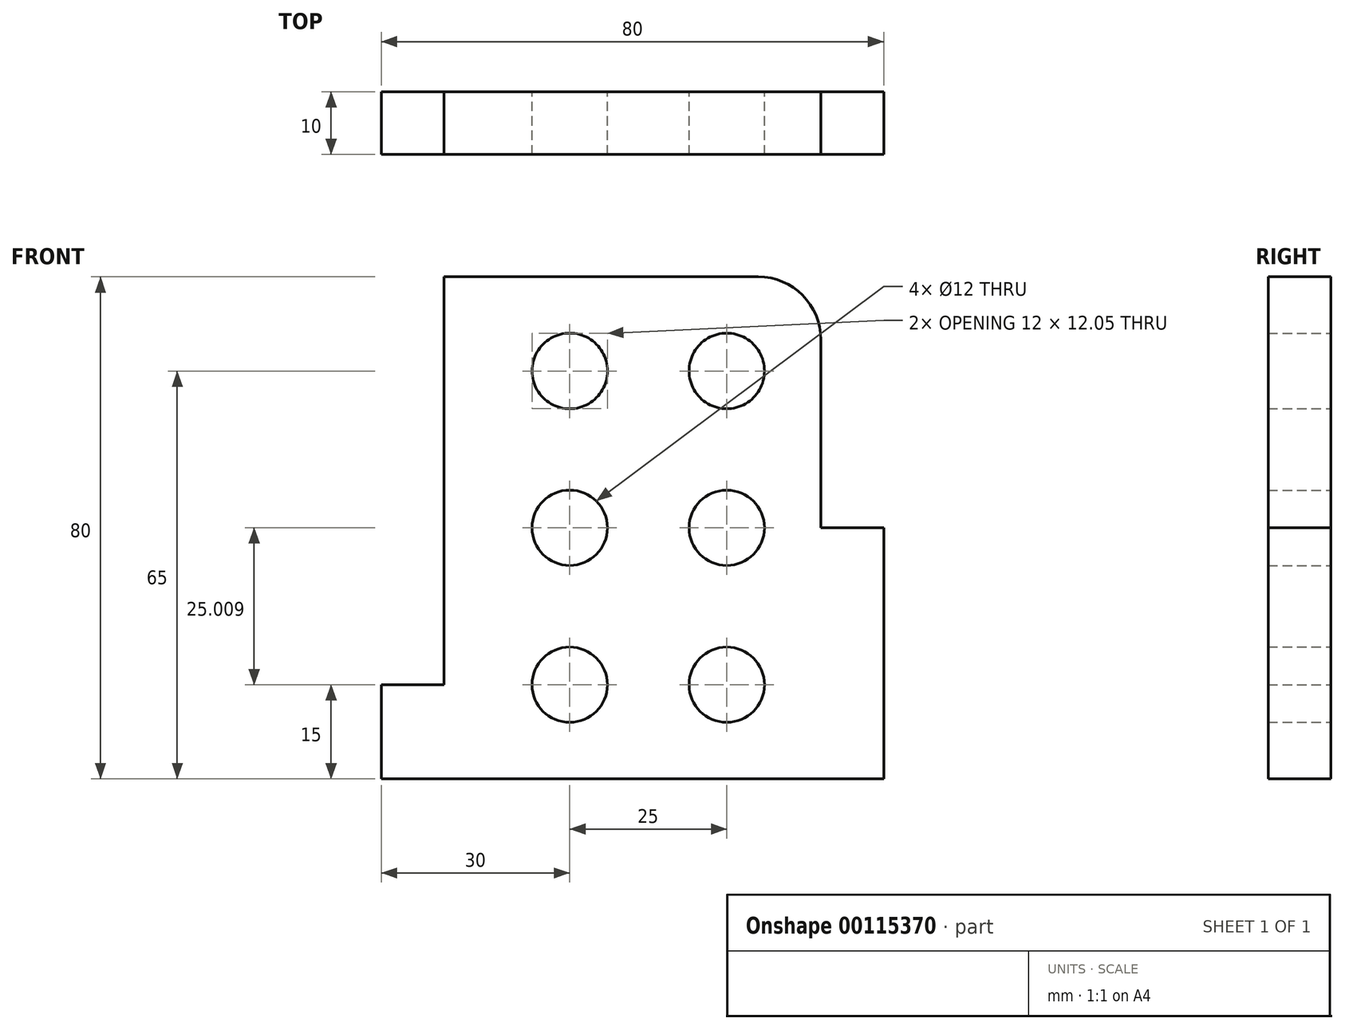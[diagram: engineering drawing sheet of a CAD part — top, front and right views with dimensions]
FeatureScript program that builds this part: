
annotation { "Feature Type Name" : "Feature", "Feature Type Description" : "" }
export const myFeature = defineFeature(function(context is Context, id is Id, definition is map)
    precondition{}
    {
        {
            var Q0;
            Q0=qCreatedBy(makeId("Front.planeOp"),FACE);
            var sketch = newSketch(context, id + "F0", { "sketchPlane" : qUnion([Q0])});
            skLineSegment(sketch, "E0", {"start": v(0, 15) * mm, "end": v(0, 0) * mm});
            skLineSegment(sketch, "E1", {"start": v(0, 0) * mm, "end": v(80, 0) * mm});
            skLineSegment(sketch, "E2", {"start": v(80, 0) * mm, "end": v(80, 40) * mm});
            skLineSegment(sketch, "E3", {"start": v(80, 40) * mm, "end": v(70, 40) * mm});
            skLineSegment(sketch, "E4", {"start": v(70, 40) * mm, "end": v(70, 70) * mm});
            skLineSegment(sketch, "E5", {"start": v(0, 15) * mm, "end": v(10, 15) * mm});
            skLineSegment(sketch, "E6", {"start": v(10, 15) * mm, "end": v(10, 80) * mm});
            skLineSegment(sketch, "E7", {"start": v(10, 80) * mm, "end": v(60, 80) * mm});
            skArc(sketch, "E8", {"start": v(60, 80) * mm, "mid": v(67.07, 77.07) * mm, "end": v(70, 70) * mm});
            skLineSegment(sketch, "E9", {"start": v(0, 15) * mm, "end": v(106.6, 15) * mm, "construction": true});
            skCircle(sketch, "E10", {"center": v(30, 15) * mm, "radius": 6 * mm});
            skCircle(sketch, "E11", {"center": v(55, 15) * mm, "radius": 6 * mm});
            skCircle(sketch, "E12.MirrorC", {"center": v(30, 65.02) * mm, "radius": 6 * mm});
            skCircle(sketch, "E13.MirrorC", {"center": v(55, 65.02) * mm, "radius": 6 * mm});
            skLineSegment(sketch, "E14.MirrorCS", {"start": v(0, 65) * mm, "end": v(106.6, 65) * mm, "construction": true});
            skCircle(sketch, "E15.MirrorC", {"center": v(30, 64.98) * mm, "radius": 6 * mm});
            skCircle(sketch, "E16.MirrorC", {"center": v(55, 64.98) * mm, "radius": 6 * mm});
            skLineSegment(sketch, "E17", {"start": v(0, 40.01) * mm, "end": v(107.1, 40) * mm, "construction": true});
            skCircle(sketch, "E18", {"center": v(30, 40) * mm, "radius": 6 * mm});
            skCircle(sketch, "E19", {"center": v(55, 40) * mm, "radius": 6 * mm});
            skLineSegment(sketch, "E20", {"start": v(30, 15) * mm, "end": v(30, 92.33) * mm, "construction": true});
            skLineSegment(sketch, "E21", {"start": v(55, 15) * mm, "end": v(55, 93.55) * mm, "construction": true});
            skLineSegment(sketch, "E22", {"start": v(0, 0) * mm, "end": v(0, 118.12) * mm, "construction": true});
            skSolve(sketch);
        }
        {
            var Q0;
            Q0=makeQuery(id+"F0.imprint","IMPRINT",FACE,{"disambiguationData":[TD([[makeQuery(id+"F0.imprint","IMPRINT",EDGE,{"derivedFrom":sQuery(id+"F0.wireOp",EDGE,"E0")}),1.0]])]});
            extrude(context, id + "F1", {"entities" : qUnion([Q0]), "depth" : 10 * mm});
        }
    });
